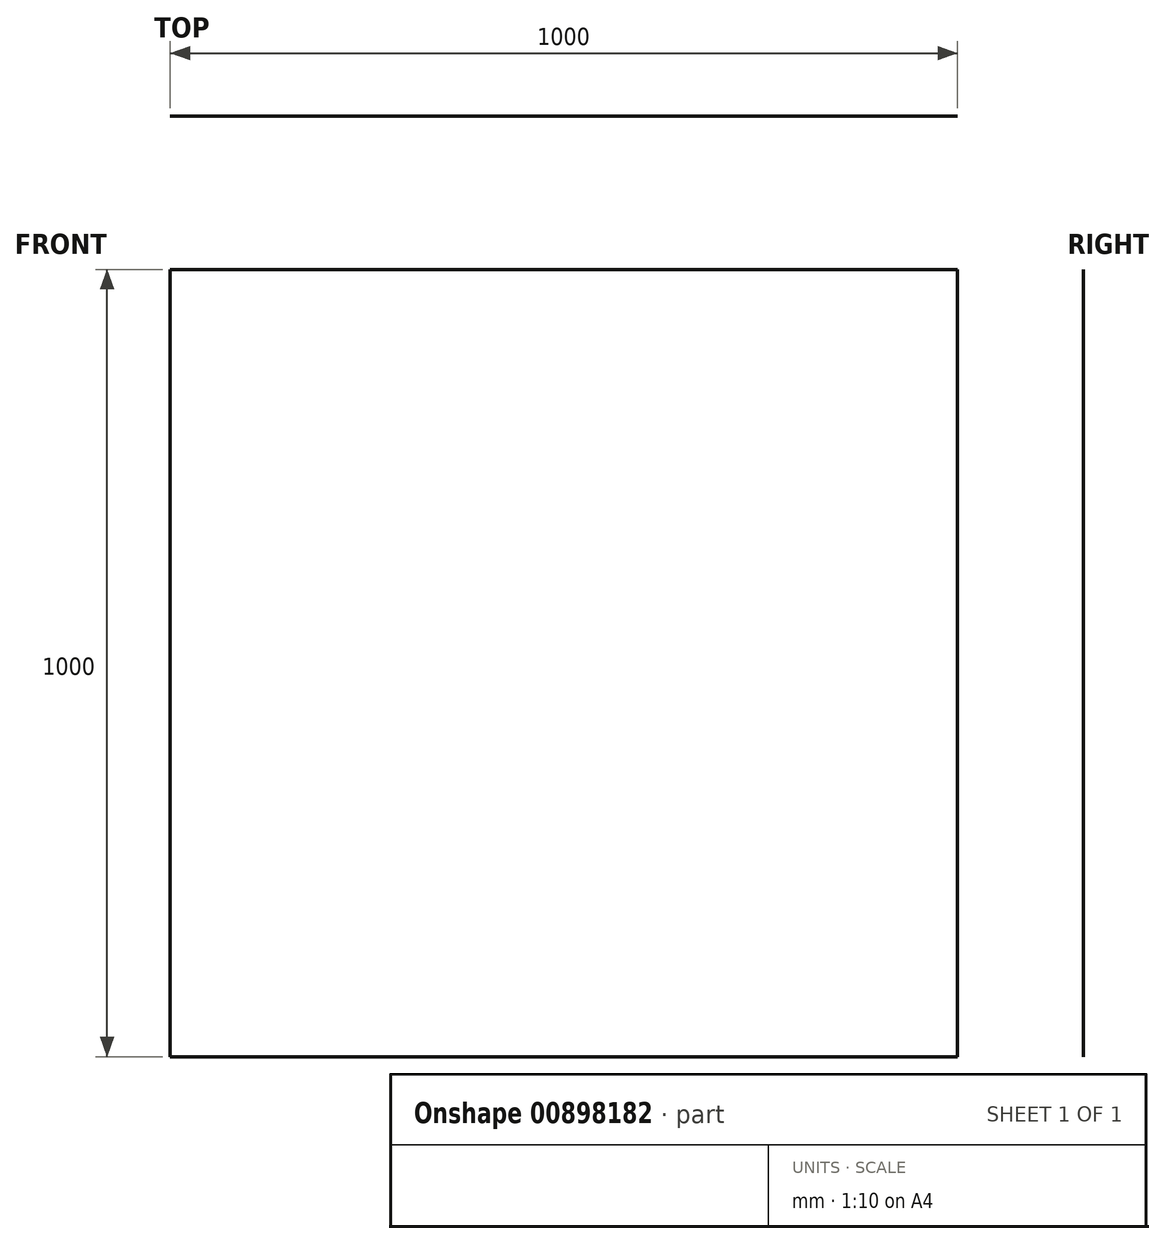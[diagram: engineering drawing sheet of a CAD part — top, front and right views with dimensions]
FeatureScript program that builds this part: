
annotation { "Feature Type Name" : "Feature", "Feature Type Description" : "" }
export const myFeature = defineFeature(function(context is Context, id is Id, definition is map)
    precondition{}
    {
        {
            var Q0;
            Q0=qCreatedBy(makeId("Top.planeOp"),FACE);
            var sketch = newSketch(context, id + "F0", { "sketchPlane" : qUnion([Q0])});
            skLineSegment(sketch, "E0", {"start": v(-500, 0) * mm, "end": v(500, 0) * mm});
            skSolve(sketch);
        }
        {
            var Q0;
            Q0=sQuery(id+"F0.wireOp",EDGE,"E0");
            extrude(context, id + "F1", {"bodyType" : ToolBodyType.SURFACE, "surfaceEntities" : qUnion([Q0]), "depth" : 1000 * mm, "offsetDistance" : 25 * mm});
        }
    });
